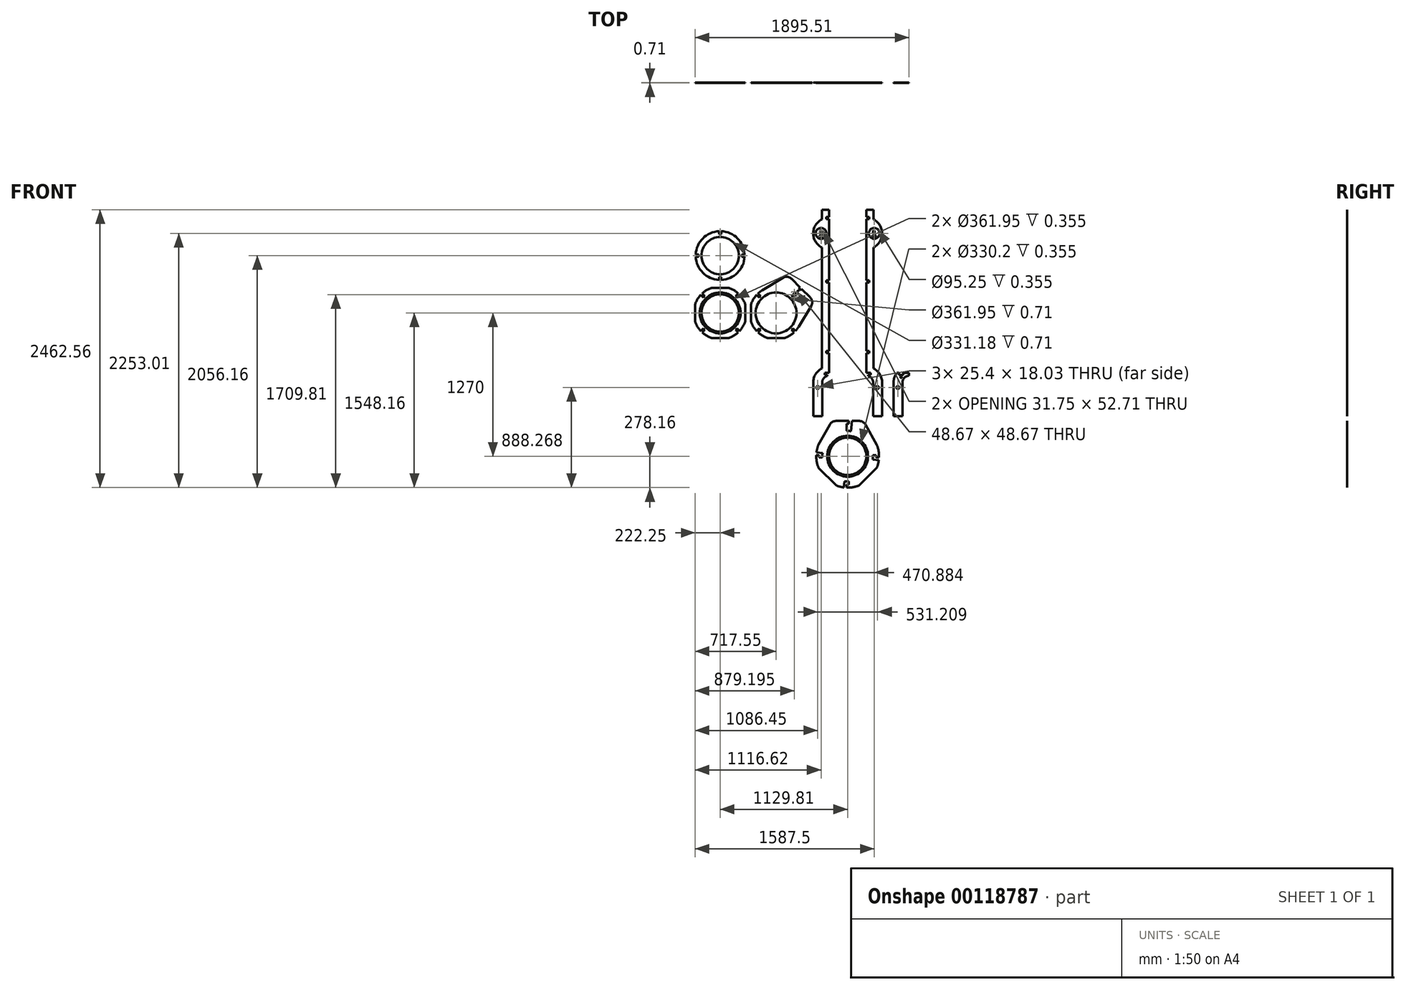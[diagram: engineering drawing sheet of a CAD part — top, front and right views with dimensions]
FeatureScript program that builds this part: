
annotation { "Feature Type Name" : "Feature", "Feature Type Description" : "" }
export const myFeature = defineFeature(function(context is Context, id is Id, definition is map)
    precondition{}
    {
        {
            assignVariable(context, id + "F0", {"name" : "thick", "anyValue" : 0.71});
        }
        {
            var Q0;
            Q0=qCreatedBy(makeId("Front.planeOp"),FACE);
            var sketch = newSketch(context, id + "F1", { "sketchPlane" : qUnion([Q0])});
            skArc(sketch, "E0", {"start": v(-76.2, 222.25) * mm, "mid": v(-166.13, 166.13) * mm, "end": v(-222.25, 76.2) * mm});
            skCircle(sketch, "E1.0", {"center": v(0, 0) * mm, "radius": 180.98 * mm});
            skCircle(sketch, "E2.0", {"center": v(0, 0) * mm, "radius": 165.1 * mm});
            skLineSegment(sketch, "E3", {"start": v(-166.13, 166.13) * mm, "end": v(166.13, -166.13) * mm, "construction": true});
            skLineSegment(sketch, "E4", {"start": v(0, 0) * mm, "end": v(-234.95, 0) * mm, "construction": true});
            skLineSegment(sketch, "E5.MirrorCS", {"start": v(-166.13, -166.13) * mm, "end": v(166.13, 166.13) * mm, "construction": true});
            skLineSegment(sketch, "E6.0", {"start": v(-159.64, 172.39) * mm, "end": v(-137.3, 150.06) * mm});
            skLineSegment(sketch, "E7.0", {"start": v(-172.39, 159.64) * mm, "end": v(-150.06, 137.3) * mm});
            skLineSegment(sketch, "E8", {"start": v(-137.3, 150.06) * mm, "end": v(-150.06, 137.3) * mm});
            skPoint(sketch, "E9", {"position": v(-143.68, 143.68) * mm});
            skLineSegment(sketch, "E10.1.0", {"start": v(-172.39, -159.64) * mm, "end": v(-150.06, -137.3) * mm});
            skLineSegment(sketch, "E10.1.1", {"start": v(-150.06, -137.3) * mm, "end": v(-137.3, -150.06) * mm});
            skLineSegment(sketch, "E10.1.2", {"start": v(-159.64, -172.39) * mm, "end": v(-137.3, -150.06) * mm});
            skLineSegment(sketch, "E10.2.0", {"start": v(159.64, -172.39) * mm, "end": v(137.3, -150.06) * mm});
            skLineSegment(sketch, "E10.2.1", {"start": v(137.3, -150.06) * mm, "end": v(150.06, -137.3) * mm});
            skLineSegment(sketch, "E10.2.2", {"start": v(172.39, -159.64) * mm, "end": v(150.06, -137.3) * mm});
            skLineSegment(sketch, "E10.3.0", {"start": v(172.39, 159.64) * mm, "end": v(150.06, 137.3) * mm});
            skLineSegment(sketch, "E10.3.1", {"start": v(150.06, 137.3) * mm, "end": v(137.3, 150.06) * mm});
            skLineSegment(sketch, "E10.3.2", {"start": v(159.64, 172.39) * mm, "end": v(137.3, 150.06) * mm});
            skLineSegment(sketch, "E11", {"start": v(-222.25, 76.2) * mm, "end": v(-222.25, -76.2) * mm});
            skLineSegment(sketch, "E12.1.0", {"start": v(-76.2, -222.25) * mm, "end": v(76.2, -222.25) * mm});
            skLineSegment(sketch, "E12.2.0", {"start": v(222.25, -76.2) * mm, "end": v(222.25, 76.2) * mm});
            skLineSegment(sketch, "E12.3.0", {"start": v(76.2, 222.25) * mm, "end": v(-76.2, 222.25) * mm});
            skArc(sketch, "E13.trimOffspring", {"start": v(222.25, 76.2) * mm, "mid": v(166.13, 166.13) * mm, "end": v(76.2, 222.25) * mm});
            skArc(sketch, "E14.trimOffspring", {"start": v(76.2, -222.25) * mm, "mid": v(166.13, -166.13) * mm, "end": v(222.25, -76.2) * mm});
            skArc(sketch, "E15.trimOffspring", {"start": v(-222.25, -76.2) * mm, "mid": v(-166.13, -166.13) * mm, "end": v(-76.2, -222.25) * mm});
            skLineSegment(sketch, "E16", {"start": v(247.65, 76.2) * mm, "end": v(247.65, -76.2) * mm, "construction": true});
            skLineSegment(sketch, "E17.MirrorCS", {"start": v(645.36, -137.3) * mm, "end": v(632.6, -150.06) * mm});
            skPoint(sketch, "E18.MirrorP", {"position": v(495.3, 0) * mm});
            skLineSegment(sketch, "E19.MirrorCS", {"start": v(358, -150.06) * mm, "end": v(345.24, -137.3) * mm});
            skLineSegment(sketch, "E20.MirrorCS", {"start": v(345.24, 137.3) * mm, "end": v(358, 150.06) * mm});
            skLineSegment(sketch, "E21.MirrorCS", {"start": v(335.66, 172.39) * mm, "end": v(358, 150.06) * mm});
            skLineSegment(sketch, "E22.MirrorCS", {"start": v(571.5, -222.25) * mm, "end": v(419.1, -222.25) * mm});
            skArc(sketch, "E23.MirrorCS", {"start": v(273.05, 76.2) * mm, "mid": v(329.17, 166.13) * mm, "end": v(419.1, 222.25) * mm});
            skLineSegment(sketch, "E24.MirrorCS", {"start": v(667.69, -159.64) * mm, "end": v(645.36, -137.3) * mm});
            skLineSegment(sketch, "E25.MirrorCS", {"start": v(273.05, -76.2) * mm, "end": v(273.05, 76.2) * mm});
            skLineSegment(sketch, "E26.MirrorCS", {"start": v(661.43, -166.13) * mm, "end": v(329.17, 166.13) * mm, "construction": true});
            skArc(sketch, "E27.MirrorCS", {"start": v(717.55, -76.2) * mm, "mid": v(661.43, -166.13) * mm, "end": v(571.5, -222.25) * mm});
            skLineSegment(sketch, "E28.MirrorCS", {"start": v(322.91, -159.64) * mm, "end": v(345.24, -137.3) * mm});
            skLineSegment(sketch, "E29.MirrorCS", {"start": v(322.91, 159.64) * mm, "end": v(345.24, 137.3) * mm});
            skArc(sketch, "E30.MirrorCS", {"start": v(571.5, 222.25) * mm, "mid": v(661.43, 166.13) * mm, "end": v(717.55, 76.2) * mm});
            skLineSegment(sketch, "E31.MirrorCS", {"start": v(654.94, -172.39) * mm, "end": v(632.6, -150.06) * mm});
            skCircle(sketch, "E32.MirrorC", {"center": v(495.3, 0) * mm, "radius": 180.98 * mm});
            skLineSegment(sketch, "E33.MirrorCS", {"start": v(661.43, 166.13) * mm, "end": v(329.17, -166.13) * mm, "construction": true});
            skLineSegment(sketch, "E34.MirrorCS", {"start": v(495.3, 0) * mm, "end": v(730.25, 0) * mm, "construction": true});
            skLineSegment(sketch, "E35.MirrorCS", {"start": v(419.1, 222.25) * mm, "end": v(571.5, 222.25) * mm});
            skLineSegment(sketch, "E36.MirrorCS", {"start": v(717.55, 76.2) * mm, "end": v(717.55, -76.2) * mm});
            skCircle(sketch, "E37.MirrorC", {"center": v(495.3, 0) * mm, "radius": 165.1 * mm});
            skArc(sketch, "E38.MirrorCS", {"start": v(419.1, -222.25) * mm, "mid": v(329.17, -166.13) * mm, "end": v(273.05, -76.2) * mm});
            skLineSegment(sketch, "E39.MirrorCS", {"start": v(335.66, -172.39) * mm, "end": v(358, -150.06) * mm});
            skCircle(sketch, "E40", {"center": v(0, 508) * mm, "radius": 229.1 * mm, "construction": true});
            skPoint(sketch, "E40.centerSnap0", {"position": v(0, 222.25) * mm});
            skCircle(sketch, "E41.0", {"center": v(0, 508) * mm, "radius": 216.4 * mm});
            skCircle(sketch, "E42.0", {"center": v(0, 508) * mm, "radius": 165.6 * mm});
            skLineSegment(sketch, "E43.bottom", {"start": v(9.02, 724.2) * mm, "end": v(-9.02, 724.2) * mm});
            skLineSegment(sketch, "E43.top", {"start": v(9.02, 699) * mm, "end": v(-9.02, 699) * mm});
            skLineSegment(sketch, "E43.left", {"start": v(9.02, 724.2) * mm, "end": v(9.02, 699) * mm});
            skLineSegment(sketch, "E43.right", {"start": v(-9.02, 724.2) * mm, "end": v(-9.02, 699) * mm});
            skPoint(sketch, "E43.middle", {"position": v(0, 711.6) * mm});
            skLineSegment(sketch, "E44.1.0", {"start": v(-216.2, 498.98) * mm, "end": v(-191, 498.98) * mm});
            skLineSegment(sketch, "E44.1.1", {"start": v(-216.2, 517.02) * mm, "end": v(-191, 517.02) * mm});
            skLineSegment(sketch, "E44.1.2", {"start": v(-191, 517.02) * mm, "end": v(-191, 498.98) * mm});
            skLineSegment(sketch, "E44.2.0", {"start": v(9.02, 291.8) * mm, "end": v(9.02, 317) * mm});
            skLineSegment(sketch, "E44.2.1", {"start": v(-9.02, 291.8) * mm, "end": v(-9.02, 317) * mm});
            skLineSegment(sketch, "E44.2.2", {"start": v(-9.02, 317) * mm, "end": v(9.02, 317) * mm});
            skLineSegment(sketch, "E44.3.0", {"start": v(216.2, 517.02) * mm, "end": v(191, 517.02) * mm});
            skLineSegment(sketch, "E44.3.1", {"start": v(216.2, 498.98) * mm, "end": v(191, 498.98) * mm});
            skLineSegment(sketch, "E44.3.2", {"start": v(191, 498.98) * mm, "end": v(191, 517.02) * mm});
            skLineSegment(sketch, "E45.bottom", {"start": v(1295.4, 914.4) * mm, "end": v(1358.9, 914.4) * mm});
            skLineSegment(sketch, "E45.left", {"start": v(1295.4, 914.4) * mm, "end": v(1295.4, -555.62) * mm});
            skLineSegment(sketch, "E45.right", {"start": v(1358.9, 914.4) * mm, "end": v(1358.9, 829.28) * mm});
            skPoint(sketch, "E45.middle", {"position": v(1327.15, 0) * mm});
            skArc(sketch, "E46", {"start": v(1355.73, -615.95) * mm, "mid": v(1338.06, -573.3) * mm, "end": v(1295.4, -555.62) * mm});
            skArc(sketch, "E47.0", {"start": v(1435.1, -615.95) * mm, "mid": v(1414.54, -543) * mm, "end": v(1358.9, -491.52) * mm});
            skArc(sketch, "E48", {"start": v(1358.9, 580.42) * mm, "mid": v(1435.1, 704.85) * mm, "end": v(1358.9, 829.28) * mm});
            skLineSegment(sketch, "E49.trimOffspring", {"start": v(1358.9, 580.42) * mm, "end": v(1358.9, -491.52) * mm});
            skCircle(sketch, "E50", {"center": v(1365.25, 704.85) * mm, "radius": 47.63 * mm});
            skLineSegment(sketch, "E51", {"start": v(1295.4, 704.85) * mm, "end": v(1435.1, 704.85) * mm, "construction": true});
            skLineSegment(sketch, "E52.bottom", {"start": v(1369.38, 731.2) * mm, "end": v(1361.12, 731.2) * mm});
            skLineSegment(sketch, "E52.top", {"start": v(1369.38, 686.75) * mm, "end": v(1361.12, 686.75) * mm});
            skLineSegment(sketch, "E52.left", {"start": v(1369.38, 731.2) * mm, "end": v(1369.38, 686.75) * mm});
            skLineSegment(sketch, "E52.right", {"start": v(1361.12, 731.2) * mm, "end": v(1361.12, 686.75) * mm});
            skLineSegment(sketch, "E53.bottom", {"start": v(1349.37, 686.75) * mm, "end": v(1381.12, 686.75) * mm});
            skLineSegment(sketch, "E53.top", {"start": v(1349.37, 678.5) * mm, "end": v(1381.12, 678.5) * mm});
            skLineSegment(sketch, "E53.left", {"start": v(1349.37, 686.75) * mm, "end": v(1349.37, 678.5) * mm});
            skLineSegment(sketch, "E53.right", {"start": v(1381.12, 686.75) * mm, "end": v(1381.12, 678.5) * mm});
            skPoint(sketch, "E53.middle", {"position": v(1365.25, 682.63) * mm});
            skPoint(sketch, "E53.middle.positionSnap0", {"position": v(1365.25, 686.75) * mm});
            skPoint(sketch, "E53.cornerSnap0", {"position": v(1365.25, 686.75) * mm});
            skPoint(sketch, "E53.centerSnap0", {"position": v(1365.25, 686.75) * mm});
            skLineSegment(sketch, "E54", {"start": v(1361.12, 731.2) * mm, "end": v(1349.37, 719.14) * mm});
            skLineSegment(sketch, "E55", {"start": v(1349.37, 719.14) * mm, "end": v(1355.29, 713.38) * mm});
            skLineSegment(sketch, "E56", {"start": v(1355.29, 713.38) * mm, "end": v(1361.12, 719.37) * mm});
            skLineSegment(sketch, "E57", {"start": v(1365.25, 731.2) * mm, "end": v(1365.25, 678.5) * mm, "construction": true});
            skLineSegment(sketch, "E58.MirrorCS", {"start": v(1295.4, -531.24) * mm, "end": v(1333, -531.24) * mm});
            skLineSegment(sketch, "E59.MirrorCS", {"start": v(1333, -549.27) * mm, "end": v(1310.78, -549.27) * mm});
            skLineSegment(sketch, "E60.MirrorCS", {"start": v(1333, -531.24) * mm, "end": v(1333, -549.27) * mm});
            skLineSegment(sketch, "E61.MirrorCS", {"start": v(1310.78, -549.27) * mm, "end": v(1310.78, -557.62) * mm});
            skLineSegment(sketch, "E62.bottom", {"start": v(1295.4, 850.9) * mm, "end": v(1320.8, 850.9) * mm});
            skLineSegment(sketch, "E62.top", {"start": v(1295.4, 832.87) * mm, "end": v(1320.8, 832.87) * mm});
            skLineSegment(sketch, "E62.left", {"start": v(1295.4, 850.9) * mm, "end": v(1295.4, 832.87) * mm});
            skLineSegment(sketch, "E62.right", {"start": v(1320.8, 850.9) * mm, "end": v(1320.8, 832.87) * mm});
            skLineSegment(sketch, "E63.bottom", {"start": v(1295.4, 288.42) * mm, "end": v(1320.8, 288.42) * mm});
            skLineSegment(sketch, "E63.top", {"start": v(1295.4, 270.38) * mm, "end": v(1320.8, 270.38) * mm});
            skLineSegment(sketch, "E63.left", {"start": v(1295.4, 288.42) * mm, "end": v(1295.4, 270.38) * mm});
            skLineSegment(sketch, "E63.right", {"start": v(1320.8, 288.42) * mm, "end": v(1320.8, 270.38) * mm});
            skLineSegment(sketch, "E64.bottom", {"start": v(1295.4, -337.57) * mm, "end": v(1320.8, -337.57) * mm});
            skLineSegment(sketch, "E64.top", {"start": v(1295.4, -355.6) * mm, "end": v(1320.8, -355.6) * mm});
            skLineSegment(sketch, "E64.left", {"start": v(1295.4, -337.57) * mm, "end": v(1295.4, -355.6) * mm});
            skLineSegment(sketch, "E64.right", {"start": v(1320.8, -337.57) * mm, "end": v(1320.8, -355.6) * mm});
            skLineSegment(sketch, "E65", {"start": v(1129.8, 914.4) * mm, "end": v(1129.8, -355.6) * mm, "construction": true});
            skLineSegment(sketch, "E66", {"start": v(1129.8, 279.4) * mm, "end": v(1320.8, 279.4) * mm, "construction": true});
            skCircle(sketch, "E67.MirrorC", {"center": v(894.37, 704.85) * mm, "radius": 47.63 * mm});
            skLineSegment(sketch, "E68.MirrorCS", {"start": v(964.22, 850.9) * mm, "end": v(938.82, 850.9) * mm});
            skLineSegment(sketch, "E69.MirrorCS", {"start": v(964.22, 270.38) * mm, "end": v(938.82, 270.38) * mm});
            skLineSegment(sketch, "E70.MirrorCS", {"start": v(938.82, 288.42) * mm, "end": v(938.82, 270.38) * mm});
            skLineSegment(sketch, "E71.MirrorCS", {"start": v(964.22, 288.42) * mm, "end": v(964.22, 270.38) * mm});
            skLineSegment(sketch, "E72.MirrorCS", {"start": v(964.22, 832.87) * mm, "end": v(938.82, 832.87) * mm});
            skLineSegment(sketch, "E73.MirrorCS", {"start": v(964.22, 850.9) * mm, "end": v(964.22, 832.87) * mm});
            skLineSegment(sketch, "E74.MirrorCS", {"start": v(964.22, -337.57) * mm, "end": v(938.82, -337.57) * mm});
            skLineSegment(sketch, "E75.MirrorCS", {"start": v(938.82, 850.9) * mm, "end": v(938.82, 832.87) * mm});
            skLineSegment(sketch, "E76.MirrorCS", {"start": v(964.22, 288.42) * mm, "end": v(938.82, 288.42) * mm});
            skLineSegment(sketch, "E77.MirrorCS", {"start": v(900.72, 914.4) * mm, "end": v(900.72, 829.28) * mm});
            skLineSegment(sketch, "E78.MirrorCS", {"start": v(964.22, -355.6) * mm, "end": v(938.82, -355.6) * mm});
            skLineSegment(sketch, "E79.MirrorCS", {"start": v(964.22, -337.57) * mm, "end": v(964.22, -355.6) * mm});
            skLineSegment(sketch, "E80.MirrorCS", {"start": v(938.82, -337.57) * mm, "end": v(938.82, -355.6) * mm});
            skLineSegment(sketch, "E81.MirrorCS", {"start": v(964.22, 914.4) * mm, "end": v(900.72, 914.4) * mm});
            skLineSegment(sketch, "E82.MirrorCS", {"start": v(964.22, 704.85) * mm, "end": v(824.52, 704.85) * mm, "construction": true});
            skLineSegment(sketch, "E83.MirrorCS", {"start": v(900.72, 580.42) * mm, "end": v(900.72, -491.52) * mm});
            skPoint(sketch, "E84.MirrorP", {"position": v(932.47, 0) * mm});
            skArc(sketch, "E85.MirrorCS", {"start": v(900.72, 580.42) * mm, "mid": v(824.52, 704.85) * mm, "end": v(900.72, 829.28) * mm});
            skLineSegment(sketch, "E86.MirrorCS", {"start": v(964.22, 914.4) * mm, "end": v(964.22, -555.62) * mm});
            skLineSegment(sketch, "E87.bottom", {"start": v(898.5, 731.2) * mm, "end": v(890.24, 731.2) * mm});
            skLineSegment(sketch, "E87.top", {"start": v(898.5, 686.75) * mm, "end": v(890.24, 686.75) * mm});
            skLineSegment(sketch, "E87.left", {"start": v(898.5, 731.2) * mm, "end": v(898.5, 686.75) * mm});
            skLineSegment(sketch, "E87.right", {"start": v(890.24, 731.2) * mm, "end": v(890.24, 686.75) * mm});
            skLineSegment(sketch, "E88.bottom", {"start": v(878.5, 686.75) * mm, "end": v(910.24, 686.75) * mm});
            skLineSegment(sketch, "E88.top", {"start": v(878.5, 678.5) * mm, "end": v(910.24, 678.5) * mm});
            skLineSegment(sketch, "E88.left", {"start": v(878.5, 686.75) * mm, "end": v(878.5, 678.5) * mm});
            skLineSegment(sketch, "E88.right", {"start": v(910.24, 686.75) * mm, "end": v(910.24, 678.5) * mm});
            skPoint(sketch, "E88.middle", {"position": v(894.37, 682.63) * mm});
            skPoint(sketch, "E88.middle.positionSnap0", {"position": v(894.37, 686.75) * mm});
            skPoint(sketch, "E88.cornerSnap0", {"position": v(894.37, 686.75) * mm});
            skPoint(sketch, "E88.centerSnap0", {"position": v(894.37, 686.75) * mm});
            skLineSegment(sketch, "E89", {"start": v(890.24, 731.2) * mm, "end": v(878.5, 719.14) * mm});
            skLineSegment(sketch, "E90", {"start": v(878.5, 719.14) * mm, "end": v(884.4, 713.38) * mm});
            skLineSegment(sketch, "E91", {"start": v(884.4, 713.38) * mm, "end": v(890.24, 719.37) * mm});
            skLineSegment(sketch, "E92", {"start": v(894.37, 731.2) * mm, "end": v(894.37, 678.5) * mm, "construction": true});
            skLineSegment(sketch, "E93", {"start": v(-166.13, 166.13) * mm, "end": v(-159.76, 172.51) * mm});
            skLineSegment(sketch, "E94.0", {"start": v(-215.87, 215.87) * mm, "end": v(-209.5, 222.25) * mm, "construction": true});
            skLineSegment(sketch, "E95", {"start": v(-76.2, 222.25) * mm, "end": v(-209.5, 222.25) * mm, "construction": true});
            skPoint(sketch, "E96", {"position": v(1435.1, -615.95) * mm});
            skLineSegment(sketch, "E97", {"start": v(1435.1, -491.52) * mm, "end": v(1333, -491.52) * mm, "construction": true});
            skLineSegment(sketch, "E98", {"start": v(-215.87, 215.87) * mm, "end": v(-143.68, 143.68) * mm, "construction": true});
            skLineSegment(sketch, "E99", {"start": v(0, 508) * mm, "end": v(0, 699) * mm, "construction": true});
            skLineSegment(sketch, "E100", {"start": v(1435.1, 704.85) * mm, "end": v(1435.1, -615.95) * mm, "construction": true});
            skLineSegment(sketch, "E101", {"start": v(1355.73, -615.95) * mm, "end": v(1355.73, -914.4) * mm});
            skLineSegment(sketch, "E102", {"start": v(1355.73, -914.4) * mm, "end": v(1435.1, -914.4) * mm});
            skLineSegment(sketch, "E103", {"start": v(1435.1, -914.4) * mm, "end": v(1435.1, -615.95) * mm});
            skLineSegment(sketch, "E104.MirrorCS", {"start": v(926.6, -549.27) * mm, "end": v(948.83, -549.27) * mm});
            skLineSegment(sketch, "E105.MirrorCS", {"start": v(926.6, -531.24) * mm, "end": v(926.6, -549.27) * mm});
            skLineSegment(sketch, "E106.MirrorCS", {"start": v(948.83, -549.27) * mm, "end": v(948.83, -557.62) * mm});
            skLineSegment(sketch, "E107.MirrorCS", {"start": v(964.22, -531.24) * mm, "end": v(926.6, -531.24) * mm});
            skLineSegment(sketch, "E108.MirrorCS", {"start": v(824.52, -491.52) * mm, "end": v(926.6, -491.52) * mm, "construction": true});
            skLineSegment(sketch, "E109.MirrorCS", {"start": v(903.9, -615.95) * mm, "end": v(903.9, -914.4) * mm});
            skLineSegment(sketch, "E110.MirrorCS", {"start": v(903.9, -914.4) * mm, "end": v(824.52, -914.4) * mm});
            skLineSegment(sketch, "E111.MirrorCS", {"start": v(824.52, -914.4) * mm, "end": v(824.52, -615.95) * mm});
            skArc(sketch, "E112.MirrorCS", {"start": v(903.9, -615.95) * mm, "mid": v(921.56, -573.3) * mm, "end": v(964.22, -555.62) * mm});
            skArc(sketch, "E113.MirrorCS", {"start": v(824.52, -615.95) * mm, "mid": v(845.08, -543) * mm, "end": v(900.72, -491.52) * mm});
            skPoint(sketch, "E114.MirrorP", {"position": v(824.52, -615.95) * mm});
            skLineSegment(sketch, "E115", {"start": v(1358.9, 44.45) * mm, "end": v(1295.4, 44.45) * mm, "construction": true});
            skLineSegment(sketch, "E116.bottom", {"start": v(1382.71, -650.87) * mm, "end": v(1408.11, -650.87) * mm});
            skLineSegment(sketch, "E116.top", {"start": v(1382.71, -668.9) * mm, "end": v(1408.11, -668.9) * mm});
            skLineSegment(sketch, "E116.left", {"start": v(1382.71, -650.87) * mm, "end": v(1382.71, -668.9) * mm});
            skLineSegment(sketch, "E116.right", {"start": v(1408.11, -650.87) * mm, "end": v(1408.11, -668.9) * mm});
            skLineSegment(sketch, "E117", {"start": v(1129.8, -914.4) * mm, "end": v(1129.8, -1270) * mm, "construction": true});
            skArc(sketch, "E118", {"start": v(1129.8, -1548.3) * mm, "mid": v(1408.11, -1270) * mm, "end": v(1129.8, -991.7) * mm});
            skLineSegment(sketch, "E119", {"start": v(1129.8, -1270) * mm, "end": v(1129.8, -1548.3) * mm, "construction": true});
            skLineSegment(sketch, "E120.bottom", {"start": v(1407.97, -1260.98) * mm, "end": v(1382.57, -1260.98) * mm});
            skLineSegment(sketch, "E120.top", {"start": v(1407.97, -1279.02) * mm, "end": v(1382.57, -1279.02) * mm});
            skLineSegment(sketch, "E120.left", {"start": v(1407.97, -1260.98) * mm, "end": v(1407.97, -1279.02) * mm});
            skLineSegment(sketch, "E120.right", {"start": v(1382.57, -1260.98) * mm, "end": v(1382.57, -1279.02) * mm});
            skPoint(sketch, "E120.middle", {"position": v(1395.27, -1270) * mm});
            skPoint(sketch, "E120.middle.positionSnap0", {"position": v(1408.11, -1270) * mm});
            skPoint(sketch, "E120.centerSnap0", {"position": v(1408.11, -1270) * mm});
            skLineSegment(sketch, "E121", {"start": v(1382.57, -1260.98) * mm, "end": v(1353.97, -1260.98) * mm});
            skArc(sketch, "E122", {"start": v(1352.43, -1297.68) * mm, "mid": v(1353.95, -1279.36) * mm, "end": v(1353.97, -1260.98) * mm});
            skLineSegment(sketch, "E123", {"start": v(1353.97, -1260.98) * mm, "end": v(1353.97, -1279.02) * mm});
            skLineSegment(sketch, "E124", {"start": v(1352.43, -1297.68) * mm, "end": v(1405.99, -1304.34) * mm});
            skArc(sketch, "E125", {"start": v(1129.8, -991.7) * mm, "mid": v(851.5, -1270) * mm, "end": v(1129.8, -1548.3) * mm});
            skLineSegment(sketch, "E126.1.0", {"start": v(1157.49, -1047.38) * mm, "end": v(1164.15, -993.82) * mm});
            skPoint(sketch, "E126.1.1", {"position": v(1129.8, -1004.54) * mm});
            skArc(sketch, "E126.1.3", {"start": v(1157.49, -1047.38) * mm, "mid": v(1139.17, -1045.86) * mm, "end": v(1120.8, -1045.84) * mm});
            skLineSegment(sketch, "E126.1.4", {"start": v(1120.8, -1045.84) * mm, "end": v(1138.83, -1045.84) * mm});
            skLineSegment(sketch, "E126.1.6", {"start": v(1138.83, -991.84) * mm, "end": v(1138.83, -1017.24) * mm});
            skLineSegment(sketch, "E126.1.7", {"start": v(1120.8, -991.84) * mm, "end": v(1120.8, -1017.24) * mm});
            skLineSegment(sketch, "E126.1.8", {"start": v(1120.8, -991.84) * mm, "end": v(1138.83, -991.84) * mm});
            skLineSegment(sketch, "E126.1.9", {"start": v(1120.8, -1017.24) * mm, "end": v(1138.83, -1017.24) * mm});
            skLineSegment(sketch, "E126.1.10", {"start": v(1120.8, -1017.24) * mm, "end": v(1120.8, -1045.84) * mm});
            skLineSegment(sketch, "E126.2.0", {"start": v(907.18, -1242.32) * mm, "end": v(853.63, -1235.66) * mm});
            skPoint(sketch, "E126.2.1", {"position": v(864.35, -1270) * mm});
            skPoint(sketch, "E126.2.2", {"position": v(851.5, -1270) * mm});
            skArc(sketch, "E126.2.3", {"start": v(907.18, -1242.32) * mm, "mid": v(905.66, -1260.64) * mm, "end": v(905.65, -1279.02) * mm});
            skLineSegment(sketch, "E126.2.4", {"start": v(905.65, -1279.02) * mm, "end": v(905.65, -1260.98) * mm});
            skPoint(sketch, "E126.2.5", {"position": v(851.5, -1270) * mm});
            skLineSegment(sketch, "E126.2.6", {"start": v(851.65, -1260.98) * mm, "end": v(877.05, -1260.98) * mm});
            skLineSegment(sketch, "E126.2.7", {"start": v(851.65, -1279.02) * mm, "end": v(877.05, -1279.02) * mm});
            skLineSegment(sketch, "E126.2.8", {"start": v(851.65, -1279.02) * mm, "end": v(851.65, -1260.98) * mm});
            skLineSegment(sketch, "E126.2.9", {"start": v(877.05, -1279.02) * mm, "end": v(877.05, -1260.98) * mm});
            skLineSegment(sketch, "E126.2.10", {"start": v(877.05, -1279.02) * mm, "end": v(905.65, -1279.02) * mm});
            skLineSegment(sketch, "E126.3.0", {"start": v(1102.13, -1492.62) * mm, "end": v(1095.47, -1546.18) * mm});
            skPoint(sketch, "E126.3.1", {"position": v(1129.8, -1535.46) * mm});
            skPoint(sketch, "E126.3.2", {"position": v(1129.8, -1548.3) * mm});
            skArc(sketch, "E126.3.3", {"start": v(1102.13, -1492.62) * mm, "mid": v(1120.44, -1494.14) * mm, "end": v(1138.83, -1494.16) * mm});
            skLineSegment(sketch, "E126.3.4", {"start": v(1138.83, -1494.16) * mm, "end": v(1120.8, -1494.16) * mm});
            skPoint(sketch, "E126.3.5", {"position": v(1129.8, -1548.3) * mm});
            skLineSegment(sketch, "E126.3.6", {"start": v(1120.8, -1548.16) * mm, "end": v(1120.8, -1522.76) * mm});
            skLineSegment(sketch, "E126.3.7", {"start": v(1138.83, -1548.16) * mm, "end": v(1138.83, -1522.76) * mm});
            skLineSegment(sketch, "E126.3.8", {"start": v(1138.83, -1548.16) * mm, "end": v(1120.8, -1548.16) * mm});
            skLineSegment(sketch, "E126.3.9", {"start": v(1138.83, -1522.76) * mm, "end": v(1120.8, -1522.76) * mm});
            skLineSegment(sketch, "E126.3.10", {"start": v(1138.83, -1522.76) * mm, "end": v(1138.83, -1494.16) * mm});
            skCircle(sketch, "E127", {"center": v(1129.8, -1270) * mm, "radius": 180.98 * mm});
            skCircle(sketch, "E128", {"center": v(1129.8, -1270) * mm, "radius": 165.1 * mm});
            skLineSegment(sketch, "E129", {"start": v(1129.8, -1270) * mm, "end": v(1294.9, -1270) * mm, "construction": true});
            skLineSegment(sketch, "E130", {"start": v(394.26, 222.25) * mm, "end": v(717.55, -101.04) * mm, "construction": true});
            skLineSegment(sketch, "E131", {"start": v(329.17, -166.13) * mm, "end": v(715.32, 220.02) * mm, "construction": true});
            skLineSegment(sketch, "E132", {"start": v(715.32, 220.02) * mm, "end": v(633.73, 301.6) * mm});
            skLineSegment(sketch, "E133", {"start": v(715.32, 220.02) * mm, "end": v(796.9, 138.43) * mm});
            skLineSegment(sketch, "E134", {"start": v(372.02, 200) * mm, "end": v(556.01, 311.07) * mm});
            skLineSegment(sketch, "E135", {"start": v(394.26, 222.25) * mm, "end": v(372.02, 200) * mm, "construction": true});
            skLineSegment(sketch, "E136.MirrorCS", {"start": v(717.55, -101.04) * mm, "end": v(695.3, -123.28) * mm, "construction": true});
            skLineSegment(sketch, "E137", {"start": v(806.37, 60.71) * mm, "end": v(695.3, -123.28) * mm});
            skPoint(sketch, "E138.visualSharp", {"position": v(598.57, 336.76) * mm});
            skArc(sketch, "E138.filletArc", {"start": v(633.73, 301.6) * mm, "mid": v(596.5, 319.74) * mm, "end": v(556.01, 311.07) * mm});
            skPoint(sketch, "E139.visualSharp", {"position": v(832.06, 103.27) * mm});
            skArc(sketch, "E139.filletArc", {"start": v(806.37, 60.71) * mm, "mid": v(815.04, 101.2) * mm, "end": v(796.9, 138.43) * mm});
            skPoint(sketch, "E140", {"position": v(638.98, 143.68) * mm});
            skLineSegment(sketch, "E141", {"start": v(632.6, 150.06) * mm, "end": v(708.94, 226.4) * mm});
            skLineSegment(sketch, "E142", {"start": v(645.36, 137.3) * mm, "end": v(721.7, 213.64) * mm});
            skLineSegment(sketch, "E143.MirrorCS", {"start": v(851.5, -650.87) * mm, "end": v(851.5, -668.9) * mm});
            skLineSegment(sketch, "E144.MirrorCS", {"start": v(876.9, -650.87) * mm, "end": v(876.9, -668.9) * mm});
            skLineSegment(sketch, "E145.MirrorCS", {"start": v(876.9, -650.87) * mm, "end": v(851.5, -650.87) * mm});
            skLineSegment(sketch, "E146.MirrorCS", {"start": v(876.9, -668.9) * mm, "end": v(851.5, -668.9) * mm});
            skLineSegment(sketch, "E147", {"start": v(1485.9, -491.52) * mm, "end": v(1485.9, -615.95) * mm, "construction": true});
            skLineSegment(sketch, "E148.MirrorCS", {"start": v(1563.69, -650.87) * mm, "end": v(1563.69, -668.9) * mm});
            skLineSegment(sketch, "E149.MirrorCS", {"start": v(1589.09, -650.87) * mm, "end": v(1589.09, -668.9) * mm});
            skLineSegment(sketch, "E150.MirrorCS", {"start": v(1589.09, -650.87) * mm, "end": v(1563.69, -650.87) * mm});
            skLineSegment(sketch, "E151.MirrorCS", {"start": v(1616.07, -615.95) * mm, "end": v(1616.07, -914.4) * mm});
            skLineSegment(sketch, "E152.MirrorCS", {"start": v(1536.7, -914.4) * mm, "end": v(1536.7, -615.95) * mm});
            skPoint(sketch, "E153.MirrorP", {"position": v(1536.7, -615.95) * mm});
            skArc(sketch, "E154.MirrorCS", {"start": v(1616.08, -615.95) * mm, "mid": v(1633.74, -573.3) * mm, "end": v(1676.4, -555.63) * mm});
            skLineSegment(sketch, "E155.MirrorCS", {"start": v(1589.09, -668.9) * mm, "end": v(1563.69, -668.9) * mm});
            skLineSegment(sketch, "E156.MirrorCS", {"start": v(1616.07, -914.4) * mm, "end": v(1536.7, -914.4) * mm});
            skPoint(sketch, "E157.MirrorCS.start.orphan", {"position": v(1676.4, -531.24) * mm});
            skPoint(sketch, "E158.orphan", {"position": v(1676.4, -555.62) * mm});
            skArc(sketch, "E159.MirrorCS", {"start": v(1536.7, -615.95) * mm, "mid": v(1544.05, -571.24) * mm, "end": v(1565.31, -531.24) * mm});
            skPoint(sketch, "E160.orphan", {"position": v(1612.9, -491.52) * mm});
            skLineSegment(sketch, "E161.MirrorCS", {"start": v(632.6, 150.06) * mm, "end": v(645.36, 137.3) * mm});
            skLineSegment(sketch, "E162", {"start": v(1565.31, -531.24) * mm, "end": v(1673.26, -531.24) * mm});
            skLineSegment(sketch, "E163", {"start": v(1673.26, -531.24) * mm, "end": v(1673.26, -555.7) * mm});
            skLineSegment(sketch, "E164", {"start": v(1673.26, -543.47) * mm, "end": v(1563.69, -543.47) * mm, "construction": true});
            skCircle(sketch, "E165.0", {"center": v(1129.8, -1270) * mm, "radius": 203.2 * mm, "construction": true});
            skLineSegment(sketch, "E166", {"start": v(1129.8, -1066.8) * mm, "end": v(1129.8, -957.23) * mm, "construction": true});
            skLineSegment(sketch, "E167.bottom", {"start": v(1120.8, -957.23) * mm, "end": v(1138.83, -957.23) * mm});
            skLineSegment(sketch, "E167.top", {"start": v(1120.8, -982.63) * mm, "end": v(1138.83, -982.63) * mm});
            skLineSegment(sketch, "E167.left", {"start": v(1120.8, -957.23) * mm, "end": v(1120.8, -982.63) * mm});
            skLineSegment(sketch, "E167.right", {"start": v(1138.83, -957.23) * mm, "end": v(1138.83, -982.63) * mm});
            skLineSegment(sketch, "E168", {"start": v(1164.15, -993.82) * mm, "end": v(1168.7, -957.23) * mm});
            skLineSegment(sketch, "E169", {"start": v(1120.8, -982.63) * mm, "end": v(1120.8, -991.84) * mm});
            skLineSegment(sketch, "E170", {"start": v(1120.8, -957.23) * mm, "end": v(1027.15, -957.23) * mm});
            skLineSegment(sketch, "E171", {"start": v(1168.7, -957.23) * mm, "end": v(1232.46, -957.23) * mm});
            skLineSegment(sketch, "E172", {"start": v(870.71, -1168.4) * mm, "end": v(1388.9, -1168.4) * mm, "construction": true});
            skLineSegment(sketch, "E173.MirrorCS", {"start": v(870.71, -1371.6) * mm, "end": v(1388.9, -1371.6) * mm, "construction": true});
            skLineSegment(sketch, "E174", {"start": v(1028.2, -1371.6) * mm, "end": v(1028.2, -1529.1) * mm, "construction": true});
            skLineSegment(sketch, "E175.MirrorCS", {"start": v(1231.4, -1371.6) * mm, "end": v(1231.4, -1529.1) * mm, "construction": true});
            skLineSegment(sketch, "E176", {"start": v(870.71, -1371.6) * mm, "end": v(1028.2, -1529.1) * mm});
            skLineSegment(sketch, "E177", {"start": v(1231.4, -1529.1) * mm, "end": v(1388.9, -1371.6) * mm});
            skLineSegment(sketch, "E178", {"start": v(870.71, -1168.4) * mm, "end": v(971.88, -989.47) * mm});
            skLineSegment(sketch, "E179", {"start": v(1287.74, -989.47) * mm, "end": v(1388.9, -1168.4) * mm});
            skPoint(sketch, "E180.visualSharp", {"position": v(990.1, -957.23) * mm});
            skArc(sketch, "E180.filletArc", {"start": v(1027.15, -957.23) * mm, "mid": v(995.15, -965.88) * mm, "end": v(971.88, -989.47) * mm});
            skPoint(sketch, "E181.visualSharp", {"position": v(1269.5, -957.23) * mm});
            skArc(sketch, "E181.filletArc", {"start": v(1287.74, -989.47) * mm, "mid": v(1264.46, -965.88) * mm, "end": v(1232.46, -957.23) * mm});
            skLineSegment(sketch, "E182", {"start": v(668.53, 185.98) * mm, "end": v(681.28, 173.23) * mm});
            skLineSegment(sketch, "E183", {"start": v(695.47, 212.92) * mm, "end": v(708.22, 200.17) * mm});
            skLineSegment(sketch, "E184", {"start": v(1622.46, -531.24) * mm, "end": v(1622.46, -549.27) * mm});
            skLineSegment(sketch, "E185", {"start": v(1622.46, -549.27) * mm, "end": v(1584.36, -549.27) * mm});
            skLineSegment(sketch, "E186", {"start": v(1584.36, -549.27) * mm, "end": v(1584.36, -531.24) * mm});
            skCircle(sketch, "E187", {"center": v(1603.41, -569.34) * mm, "radius": 5.33 * mm});
            skPoint(sketch, "E187.centerSnap0", {"position": v(1603.41, -549.27) * mm});
            skCircle(sketch, "E188", {"center": v(688.38, 193.08) * mm, "radius": 3.81 * mm});
            skSolve(sketch);
        }
        {
            var Q0;
            Q0=makeQuery(id+"F1.imprint","IMPRINT",FACE,{"disambiguationData":[TD([[makeQuery(id+"F1.imprint","IMPRINT",EDGE,{"derivedFrom":sQuery(id+"F1.wireOp",EDGE,"E42.0")}),-1.0]])]});
            var Q1;
            Q1=makeQuery(id+"F1.imprint","IMPRINT",FACE,{"disambiguationData":[TD([[makeQuery(id+"F1.imprint","IMPRINT",EDGE,{"derivedFrom":sQuery(id+"F1.wireOp",EDGE,"E1.0")}),-1.0]])]});
            var Q2;
            Q2=makeQuery(id+"F1.imprint","IMPRINT",FACE,{"disambiguationData":[TD([[makeQuery(id+"F1.imprint","IMPRINT",EDGE,{"derivedFrom":sQuery(id+"F1.wireOp",EDGE,"E17.MirrorCS")}),-1.0]])]});
            var Q3;
            {var subQ12=sQuery(id+"F1.wireOp",EDGE,"ca3a832c-03f7-4a1b-8a6c-0b75b93ac6f213.MirrorCS");Q3=makeQuery(id+"F1.imprint","IMPRINT",FACE,{"disambiguationData":[TD([[makeQuery(id+"F1.imprint","IMPRINT",EDGE,{"derivedFrom":subQ12}),1.0]])]});}
            var Q4;
            {var subQ16=sQuery(id+"F1.wireOp",EDGE,"E45.bottom");Q4=makeQuery(id+"F1.imprint","IMPRINT",FACE,{"disambiguationData":[TD([[makeQuery(id+"F1.imprint","IMPRINT",EDGE,{"derivedFrom":subQ16}),-1.0]])]});}
            var Q5;
            Q5=makeQuery(id+"F1.imprint","IMPRINT",FACE,{"disambiguationData":[TD([[makeQuery(id+"F1.imprint","IMPRINT",EDGE,{"derivedFrom":sQuery(id+"F1.wireOp",EDGE,"E67.MirrorC")}),1.0]])]});
            var Q6;
            Q6=makeQuery(id+"F1.imprint","IMPRINT",FACE,{"disambiguationData":[TD([[makeQuery(id+"F1.imprint","IMPRINT",EDGE,{"derivedFrom":sQuery(id+"F1.wireOp",EDGE,"E120.bottom")}),-1.0]])]});
            var Q7;
            Q7=makeQuery(id+"F1.imprint","IMPRINT",FACE,{"disambiguationData":[TD([[makeQuery(id+"F1.imprint","IMPRINT",EDGE,{"derivedFrom":sQuery(id+"F1.wireOp",EDGE,"E126.2.6")}),-1.0]])]});
            var Q8;
            Q8=makeQuery(id+"F1.imprint","IMPRINT",FACE,{"disambiguationData":[TD([[makeQuery(id+"F1.imprint","IMPRINT",EDGE,{"derivedFrom":sQuery(id+"F1.wireOp",EDGE,"E120.bottom")}),1.0]])]});
            var Q9;
            Q9=makeQuery(id+"F1.imprint","IMPRINT",FACE,{"disambiguationData":[TD([[makeQuery(id+"F1.imprint","IMPRINT",EDGE,{"derivedFrom":sQuery(id+"F1.wireOp",EDGE,"E126.3.6")}),-1.0]])]});
            var Q10;
            {var subQ4=sQuery(id+"F1.wireOp",EDGE,"E35.MirrorCS");Q10=makeQuery(id+"F1.imprint","IMPRINT",FACE,{"disambiguationData":[TD([[makeQuery(id+"F1.imprint","IMPRINT",EDGE,{"derivedFrom":subQ4}),1.0]])]});}
            var Q11;
            {var subQ4=sQuery(id+"F1.wireOp",EDGE,"E36.MirrorCS");Q11=makeQuery(id+"F1.imprint","IMPRINT",FACE,{"disambiguationData":[TD([[makeQuery(id+"F1.imprint","IMPRINT",EDGE,{"derivedFrom":subQ4}),1.0]])]});}
            var Q12;
            Q12=makeQuery(id+"F1.imprint","IMPRINT",FACE,{"disambiguationData":[TD([[makeQuery(id+"F1.imprint","IMPRINT",EDGE,{"derivedFrom":sQuery(id+"F1.wireOp",EDGE,"dbb929c1-fc1a-412e-868e-8f40cd9a2ffa0.MirrorCS")}),-1.0]])]});
            var Q13;
            Q13=makeQuery(id+"F1.imprint","IMPRINT",FACE,{"disambiguationData":[TD([[makeQuery(id+"F1.imprint","IMPRINT",EDGE,{"derivedFrom":sQuery(id+"F1.wireOp",EDGE,"E148.MirrorCS")}),-1.0]])]});
            var Q14;
            {var subQ4=sQuery(id+"F1.wireOp",EDGE,"E167.left");Q14=makeQuery(id+"F1.imprint","IMPRINT",FACE,{"disambiguationData":[TD([[makeQuery(id+"F1.imprint","IMPRINT",EDGE,{"derivedFrom":subQ4}),-1.0]])]});}
            var Q15;
            Q15=makeQuery(id+"F1.imprint","IMPRINT",FACE,{"disambiguationData":[TD([[makeQuery(id+"F1.imprint","IMPRINT",EDGE,{"derivedFrom":sQuery(id+"F1.wireOp",EDGE,"E167.bottom")}),-1.0]])]});
            var Q16;
            {var subQ0=sQuery(id+"F1.wireOp",EDGE,"o3xloewI-UyoQ-rHIN-BEk7-SN8hsRkfhzbm");Q16=makeQuery(id+"F1.imprint","IMPRINT",FACE,{"disambiguationData":[TD([[makeQuery(id+"F1.imprint","IMPRINT",EDGE,{"derivedFrom":subQ0}),-1.0]])]});}
            var Q17;
            {var subQ0=sQuery(id+"F1.wireOp",EDGE,"E168");Q17=makeQuery(id+"F1.imprint","IMPRINT",FACE,{"disambiguationData":[TD([[makeQuery(id+"F1.imprint","IMPRINT",EDGE,{"derivedFrom":subQ0}),-1.0]])]});}
            var Q18;
            {var subQ0=sQuery(id+"F1.wireOp",EDGE,"cLFyrrFT-fY7a-nj2Y-pLoB-14S1D6hWbuwh");Q18=makeQuery(id+"F1.imprint","IMPRINT",FACE,{"disambiguationData":[TD([[makeQuery(id+"F1.imprint","IMPRINT",EDGE,{"derivedFrom":subQ0}),1.0]])]});}
            var Q19;
            {var subQ0=sQuery(id+"F1.wireOp",EDGE,"E182");Q19=makeQuery(id+"F1.imprint","IMPRINT",FACE,{"disambiguationData":[TD([[makeQuery(id+"F1.imprint","IMPRINT",EDGE,{"derivedFrom":subQ0}),1.0]])]});}
            extrude(context, id + "F2", {"entities" : qUnion([Q0, Q1, Q2, Q3, Q4, Q5, Q6, Q7, Q8, Q9, Q10, Q11, Q12, Q13, Q14, Q15, Q16, Q17, Q18, Q19]), "depth" : (getVariable(context, 'thick')) * mm});
        }
        {
            var Q0;
            Q0=makeQuery(id+"F1.imprint","IMPRINT",FACE,{"disambiguationData":[TD([[makeQuery(id+"F1.imprint","IMPRINT",EDGE,{"derivedFrom":sQuery(id+"F1.wireOp",EDGE,"E1.0")}),1.0]])]});
            var Q1;
            Q1=makeQuery(id+"F1.imprint","IMPRINT",FACE,{"disambiguationData":[TD([[makeQuery(id+"F1.imprint","IMPRINT",EDGE,{"derivedFrom":sQuery(id+"F1.wireOp",EDGE,"E32.MirrorC")}),-1.0]])]});
            var Q2;
            Q2=makeQuery(id+"F1.imprint","IMPRINT",FACE,{"disambiguationData":[TD([[makeQuery(id+"F1.imprint","IMPRINT",EDGE,{"derivedFrom":sQuery(id+"F1.wireOp",EDGE,"ca3a832c-03f7-4a1b-8a6c-0b75b93ac6f22.MirrorCS")}),1.0]])]});
            var Q3;
            Q3=makeQuery(id+"F1.imprint","IMPRINT",FACE,{"disambiguationData":[TD([[makeQuery(id+"F1.imprint","IMPRINT",EDGE,{"derivedFrom":sQuery(id+"F1.wireOp",EDGE,"E50")}),1.0]])]});
            var Q4;
            Q4=makeQuery(id+"F1.imprint","IMPRINT",FACE,{"disambiguationData":[TD([[makeQuery(id+"F1.imprint","IMPRINT",EDGE,{"derivedFrom":sQuery(id+"F1.wireOp",EDGE,"E67.MirrorC")}),-1.0]])]});
            var Q5;
            Q5=makeQuery(id+"F1.imprint","IMPRINT",FACE,{"disambiguationData":[TD([[makeQuery(id+"F1.imprint","IMPRINT",EDGE,{"derivedFrom":sQuery(id+"F1.wireOp",EDGE,"E127")}),1.0]])]});
            extrude(context, id + "F3", {"entities" : qUnion([Q0, Q1, Q2, Q3, Q4, Q5]), "operationType" : NewBodyOperationType.ADD, "depth" : (getVariable(context, 'thick') / 2) * mm});
        }
    });
